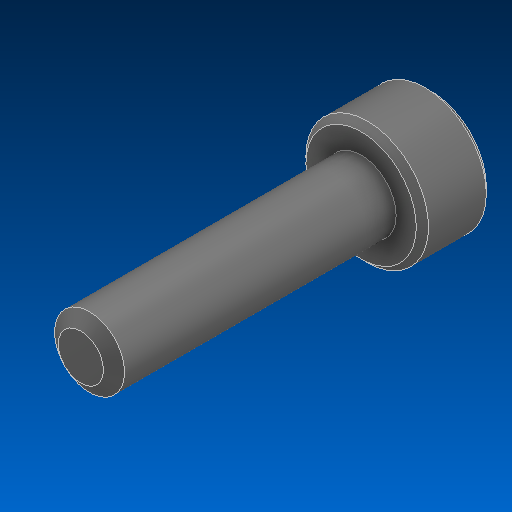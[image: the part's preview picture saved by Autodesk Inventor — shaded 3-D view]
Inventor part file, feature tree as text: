
AUTODESK INVENTOR PART (.ipt)
format: ipt  version: 2022.2 (Build 262287000, 287)  size: 126,464 bytes
history: native  units: in
note: dims shown in document units (in); Inventor stores cm internally (conversion verified against a paired STEP export)
features: chamfer x1
ambient origin geometry x8: Origin, YZ Plane, XZ Plane, XY Plane, X Axis, Y Axis, Z Axis, Center Point
bodies: Solid1 (feature_tree)
feature tree (1):
  chamfer  "Chamfer1"  [1 undecoded]
note: 1 required parameter value undecoded (feature->parameter linkage not recoverable at this tier; creation-order binding heuristic only, values carry confidence <= 0.55)
